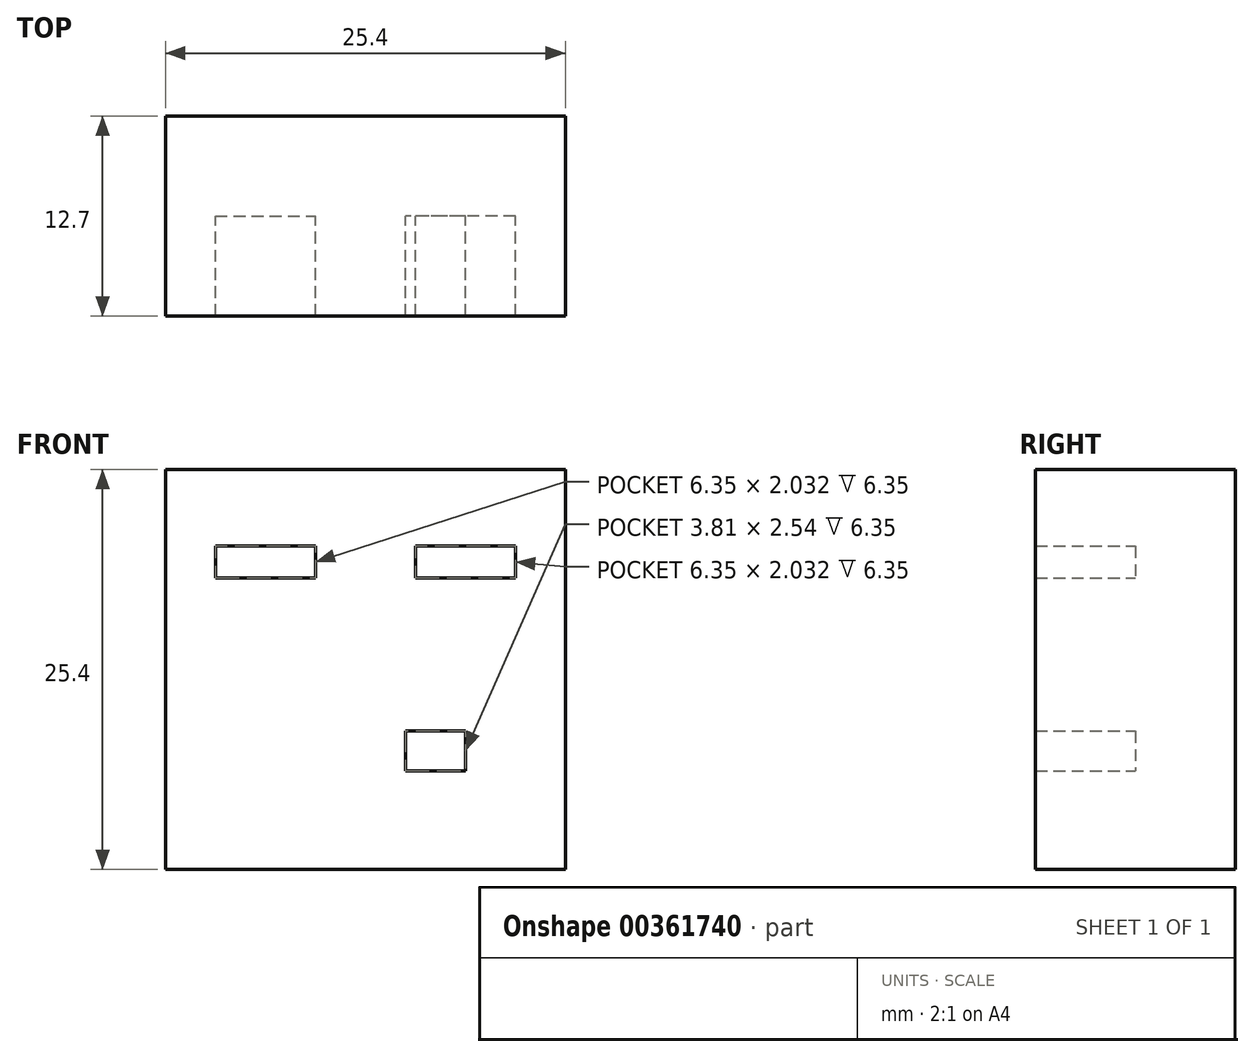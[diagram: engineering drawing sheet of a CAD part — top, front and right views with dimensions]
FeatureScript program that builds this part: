
annotation { "Feature Type Name" : "Feature", "Feature Type Description" : "" }
export const myFeature = defineFeature(function(context is Context, id is Id, definition is map)
    precondition{}
    {
        {
            var Q0;
            Q0=qCreatedBy(makeId("Front.planeOp"),FACE);
            var sketch = newSketch(context, id + "F0", { "sketchPlane" : qUnion([Q0])});
            skPoint(sketch, "E0.middle", {"position": v(0, 0) * mm});
            skLineSegment(sketch, "E1.bottom", {"start": v(12.7, 12.7) * mm, "end": v(-12.7, 12.7) * mm});
            skLineSegment(sketch, "E1.top", {"start": v(12.7, -12.7) * mm, "end": v(-12.7, -12.7) * mm});
            skLineSegment(sketch, "E1.left", {"start": v(12.7, 12.7) * mm, "end": v(12.7, -12.7) * mm});
            skLineSegment(sketch, "E1.right", {"start": v(-12.7, 12.7) * mm, "end": v(-12.7, -12.7) * mm});
            skSolve(sketch);
        }
        {
            var Q0;
            Q0=makeQuery(id+"F0.imprint","IMPRINT",FACE,{"disambiguationData":[TD([[makeQuery(id+"F0.imprint","IMPRINT",EDGE,{"derivedFrom":sQuery(id+"F0.wireOp",EDGE,"E1.bottom")}),1.0]])]});
            extrude(context, id + "F1", {"entities" : qUnion([Q0]), "depth" : 6.35 * mm});
        }
        {
            var Q0;
            Q0=makeQuery(id+"F1.opExtrude","CAP_FACE",FACE,{"disambiguationData":[OSD([sQuery(id+"F0.wireOp",EDGE,"E1.bottom"),sQuery(id+"F0.wireOp",EDGE,"E1.top"),sQuery(id+"F0.wireOp",EDGE,"E1.left"),sQuery(id+"F0.wireOp",EDGE,"E1.right")])],"isStart":false});
            var sketch = newSketch(context, id + "F2", { "sketchPlane" : qUnion([Q0])});
            skLineSegment(sketch, "E2", {"start": v(-9.53, 7.83) * mm, "end": v(-3.17, 7.83) * mm});
            skLineSegment(sketch, "E3.MirrorCS", {"start": v(9.53, 7.83) * mm, "end": v(3.17, 7.83) * mm});
            skLineSegment(sketch, "E4", {"start": v(9.53, 7.83) * mm, "end": v(9.53, 5.8) * mm});
            skLineSegment(sketch, "E5.MirrorCS", {"start": v(-9.53, 7.83) * mm, "end": v(-9.53, 5.8) * mm});
            skLineSegment(sketch, "E6", {"start": v(-3.17, 7.83) * mm, "end": v(-3.17, 5.8) * mm});
            skLineSegment(sketch, "E7", {"start": v(-3.17, 5.8) * mm, "end": v(-9.53, 5.8) * mm});
            skLineSegment(sketch, "E8", {"start": v(3.17, 7.83) * mm, "end": v(3.17, 5.8) * mm});
            skLineSegment(sketch, "E9", {"start": v(3.17, 5.8) * mm, "end": v(9.53, 5.8) * mm});
            skLineSegment(sketch, "E10", {"start": v(6.35, -3.92) * mm, "end": v(2.54, -3.92) * mm});
            skLineSegment(sketch, "E11", {"start": v(2.54, -3.92) * mm, "end": v(2.54, -6.46) * mm});
            skLineSegment(sketch, "E12", {"start": v(2.54, -6.46) * mm, "end": v(6.35, -6.46) * mm});
            skLineSegment(sketch, "E13", {"start": v(6.35, -3.92) * mm, "end": v(6.35, -6.46) * mm});
            skSolve(sketch);
        }
        {
            var Q0;
            Q0=makeQuery(id+"F2.imprint","IMPRINT",FACE,{"disambiguationData":[TD([[makeQuery(id+"F2.imprint","IMPRINT",EDGE,{"derivedFrom":sQuery(id+"F2.wireOp",EDGE,"E2")}),1.0]])]});
            extrude(context, id + "F3", {"entities" : qUnion([Q0]), "operationType" : NewBodyOperationType.ADD, "depth" : 6.35 * mm});
        }
    });
